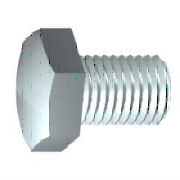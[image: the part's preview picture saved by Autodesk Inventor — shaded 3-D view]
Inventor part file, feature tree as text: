
AUTODESK INVENTOR PART (.ipt)
format: ipt  version: 2023 (Build 270158000, 158)  size: 220,160 bytes
history: native  units: mm
features: sketch x4, other x2, plane x1
ambient origin geometry x8: Origin, YZ Plane, XZ Plane, XY Plane, X Axis, Y Axis, Z Axis, Center Point
bodies: Solid1 (feature_tree)
feature tree (7):
  plane  "Work Plane1"
  sketch  "Sketch1"  dims[d6=0.6mm]
  sketch  "Sketch2"  dims[d7=14.63mm]
  sketch  "Sketch4"  dims[d9=135.0deg d10=10.0mm d11=20.0mm d13=90.0deg d14=17.0mm d15=0.0mm d16=0.6mm d17=2.0mm d18=45.0deg d19=16.0mm d20=18.475209mm d21=5.8mm d22=0.0mm d32=11.2mm d34=0.0mm d35=10.0mm d37=0.0mm d38=0.0mm d39=120.0deg d40=16.0mm d41=10.0mm d42=60.0deg d49=0.6mm d50=0.0mm]
  other  "Srf2"
  sketch  "Sketch3"  dims[d8=0.1mm]
  other  "Srf1"
